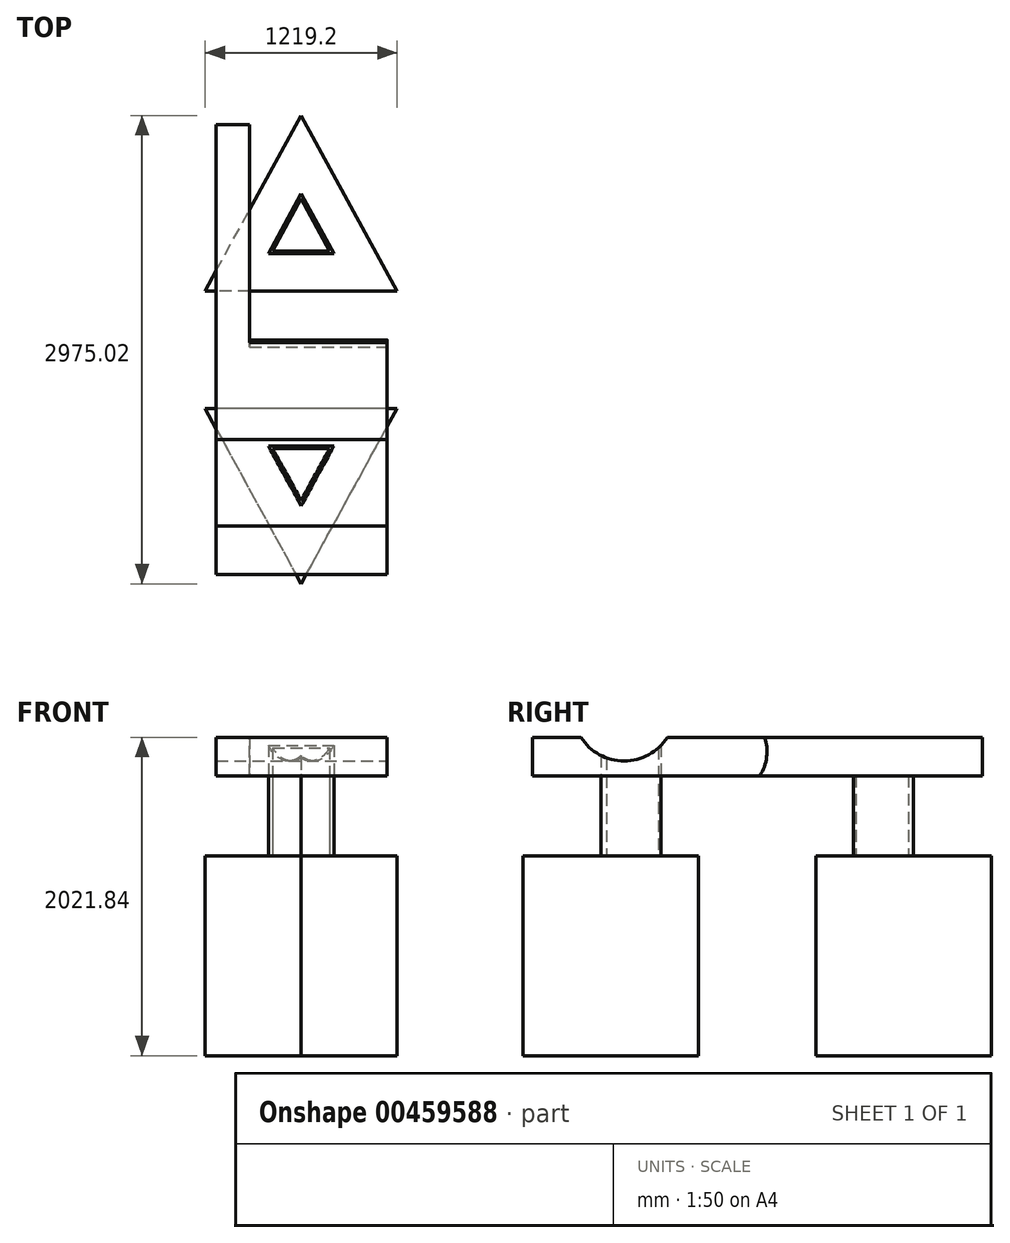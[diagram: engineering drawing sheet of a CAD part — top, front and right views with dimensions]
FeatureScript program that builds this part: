
annotation { "Feature Type Name" : "Feature", "Feature Type Description" : "" }
export const myFeature = defineFeature(function(context is Context, id is Id, definition is map)
    precondition{}
    {
        {
            var Q0;
            Q0=qCreatedBy(makeId("Top.planeOp"),FACE);
            var sketch = newSketch(context, id + "F0", { "sketchPlane" : qUnion([Q0])});
            skLineSegment(sketch, "E0", {"start": v(0, 0) * mm, "end": v(609.6, 1114.13) * mm});
            skLineSegment(sketch, "E1", {"start": v(609.6, 1114.13) * mm, "end": v(1219.2, 0) * mm});
            skLineSegment(sketch, "E2", {"start": v(1219.2, 0) * mm, "end": v(0, 0) * mm});
            skSolve(sketch);
        }
        {
            var Q0;
            Q0=makeQuery(id+"F0.imprint","IMPRINT",FACE,{"disambiguationData":[TD([[makeQuery(id+"F0.imprint","IMPRINT",EDGE,{"derivedFrom":sQuery(id+"F0.wireOp",EDGE,"E0")}),-1.0]])]});
            extrude(context, id + "F1", {"entities" : qUnion([Q0]), "depth" : 1270 * mm});
        }
        {
            var Q0;
            Q0=makeQuery(id+"F1.opExtrude","CAP_FACE",FACE,{"disambiguationData":[OSD([sQuery(id+"F0.wireOp",EDGE,"E0"),sQuery(id+"F0.wireOp",EDGE,"E1"),sQuery(id+"F0.wireOp",EDGE,"E2")])],"isStart":false});
            var sketch = newSketch(context, id + "F2", { "sketchPlane" : qUnion([Q0])});
            skLineSegment(sketch, "E3.0", {"start": v(428.51, 254) * mm, "end": v(790.69, 254) * mm});
            skLineSegment(sketch, "E3.1", {"start": v(609.6, 584.96) * mm, "end": v(428.51, 254) * mm});
            skLineSegment(sketch, "E3.2", {"start": v(790.69, 254) * mm, "end": v(609.6, 584.96) * mm});
            skLineSegment(sketch, "E4.0", {"start": v(609.6, 618.3) * mm, "end": v(401.52, 238) * mm});
            skLineSegment(sketch, "E4.1", {"start": v(817.68, 238) * mm, "end": v(609.6, 618.3) * mm});
            skLineSegment(sketch, "E4.2", {"start": v(401.52, 238) * mm, "end": v(817.68, 238) * mm});
            skSolve(sketch);
        }
        {
            var Q0;
            Q0=makeQuery(id+"F2.imprint","IMPRINT",FACE,{"disambiguationData":[TD([[makeQuery(id+"F2.imprint","IMPRINT",EDGE,{"derivedFrom":sQuery(id+"F2.wireOp",EDGE,"E3.0")}),-1.0]])]});
            extrude(context, id + "F3", {"entities" : qUnion([Q0]), "operationType" : NewBodyOperationType.ADD, "depth" : 711.2 * mm});
        }
        {
            var Q0;
            {var subQ0=sQuery(id+"F0.wireOp",EDGE,"E2");var subQ1=sQuery(id+"F0.wireOp",EDGE,"E1");var subQ2=sQuery(id+"F0.wireOp",EDGE,"E0");Q0=makeQuery(id+"F3.boolean.opBoolean","SPLIT",FACE,{"disambiguationData":[TD([makeQuery(id+"F1.opExtrude","SWEPT_FACE",FACE,{"disambiguationData":[OSD([subQ2])]})])],"derivedFrom":makeQuery(id+"F1.opExtrude","CAP_FACE",FACE,{"disambiguationData":[OSD([subQ2,subQ1,subQ0])],"isStart":false})});}
            cPlane(context, id + "F4", {"entities" : qUnion([Q0]), "cplaneType" : CPlaneType.OFFSET, "offset" : 508 * mm, "width" : 152.4 * mm, "height" : 152.4 * mm});
        }
        {
            var Q0;
            Q0=makeQuery(id+"F1.opExtrude","SWEPT_FACE",FACE,{"disambiguationData":[OSD([sQuery(id+"F0.wireOp",EDGE,"E2")])]});
            cPlane(context, id + "F5", {"entities" : qUnion([Q0]), "cplaneType" : CPlaneType.OFFSET, "offset" : 373.38 * mm, "width" : 152.4 * mm, "height" : 152.4 * mm});
        }
        {
            var Q0;
            Q0=makeQuery(id+"F1.opExtrude","SWEPT_BODY",BODY,{"disambiguationData":[OSD([sQuery(id+"F0.wireOp",EDGE,"E0"),sQuery(id+"F0.wireOp",EDGE,"E1"),sQuery(id+"F0.wireOp",EDGE,"E2")])]});
            var Q1;
            Q1=qCreatedBy(id+"F5.planeOp",FACE);
            mirror(context, id + "F6", {"entities" : qUnion([Q0]), "mirrorPlane" : qUnion([Q1])});
        }
        {
            var Q0;
            Q0=qCreatedBy(id+"F4.planeOp",FACE);
            var sketch = newSketch(context, id + "F7", { "sketchPlane" : qUnion([Q0])});
            skLineSegment(sketch, "E5.bottom", {"start": v(1156, 1055.52) * mm, "end": v(70.91, 1055.52) * mm});
            skLineSegment(sketch, "E5.top", {"start": v(1156, -1802.28) * mm, "end": v(70.91, -1802.28) * mm});
            skLineSegment(sketch, "E5.left", {"start": v(1156, 1055.52) * mm, "end": v(1156, -1802.28) * mm});
            skLineSegment(sketch, "E5.right", {"start": v(70.91, 1055.52) * mm, "end": v(70.91, -1802.28) * mm});
            skLineSegment(sketch, "E6", {"start": v(613.46, 1055.52) * mm, "end": v(613.46, -1802.28) * mm, "construction": true});
            skLineSegment(sketch, "E7", {"start": v(1156, -373.38) * mm, "end": v(70.91, -373.38) * mm, "construction": true});
            skSolve(sketch);
        }
        {
            var Q0;
            Q0=makeQuery(id+"F7.imprint","IMPRINT",FACE,{"disambiguationData":[TD([[makeQuery(id+"F7.imprint","IMPRINT",EDGE,{"derivedFrom":sQuery(id+"F7.wireOp",EDGE,"E5.bottom")}),1.0]])]});
            var Q1;
            Q1=sQuery(id+"F7.wireOp",EDGE,"E6");
            var Q2;
            Q2=sQuery(id+"F7.wireOp",EDGE,"E7");
            var Q3;
            Q3=sQuery(id+"F7.wireOp",EDGE,"E5.left");
            var Q4;
            Q4=sQuery(id+"F7.wireOp",EDGE,"E5.top");
            var Q5;
            Q5=sQuery(id+"F7.wireOp",EDGE,"E5.right");
            var Q6;
            Q6=sQuery(id+"F7.wireOp",EDGE,"E5.bottom");
            extrude(context, id + "F8", {"entities" : qUnion([Q0]), "surfaceEntities" : qUnion([Q1, Q2, Q3, Q4, Q5, Q6]), "depth" : 243.84 * mm});
        }
        {
            var Q0;
            Q0=makeQuery(id+"F8.opExtrude","SWEPT_FACE",FACE,{"disambiguationData":[OSD([sQuery(id+"F7.wireOp",EDGE,"E5.left")])]});
            var sketch = newSketch(context, id + "F9", { "sketchPlane" : qUnion([Q0])});
            skCircle(sketch, "E8", {"center": v(-1219.28, 2195.85) * mm, "radius": 324.65 * mm});
            skSolve(sketch);
        }
        {
            var Q0;
            Q0 = qSketchRegion(id + "F9", true);
            extrude(context, id + "F10", {"entities" : qUnion([Q0]), "operationType" : NewBodyOperationType.REMOVE, "oppositeDirection" : true, "depth" : 1181.1 * mm});
        }
        {
            var Q0;
            Q0=makeQuery(id+"F8.opExtrude","SWEPT_FACE",FACE,{"disambiguationData":[OSD([sQuery(id+"F7.wireOp",EDGE,"E5.left")])]});
            var sketch = newSketch(context, id + "F11", { "sketchPlane" : qUnion([Q0])});
            skCircle(sketch, "E9", {"center": v(-585.07, 1929.68) * mm, "radius": 273.48 * mm});
            skSolve(sketch);
        }
        {
            var Q0;
            {var subQ0=sQuery(id+"F11.wireOp",EDGE,"E9");var subQ2=sQuery(id+"F7.wireOp",EDGE,"E5.left");var subQ5=makeQuery(id+"F8.opExtrude","CAP_EDGE",EDGE,{"disambiguationData":[OSD([subQ2])],"isStart":true});var subQ6=makeQuery(id+"F11.imprint","INTERSECT",VERTEX,{"disambiguationData":[OD(0.0)],"derivedFrom":[subQ5,subQ0]});Q0=makeQuery(id+"F11.imprint","IMPRINT",FACE,{"disambiguationData":[TD([[makeQuery(id+"F11.imprint","IMPRINT",EDGE,{"disambiguationData":[TD([[subQ6,1.0]])],"derivedFrom":subQ5}),-1.0]])]});}
            extrude(context, id + "F12", {"entities" : qUnion([Q0]), "operationType" : NewBodyOperationType.REMOVE, "oppositeDirection" : true, "depth" : 873.76 * mm});
        }
    });
